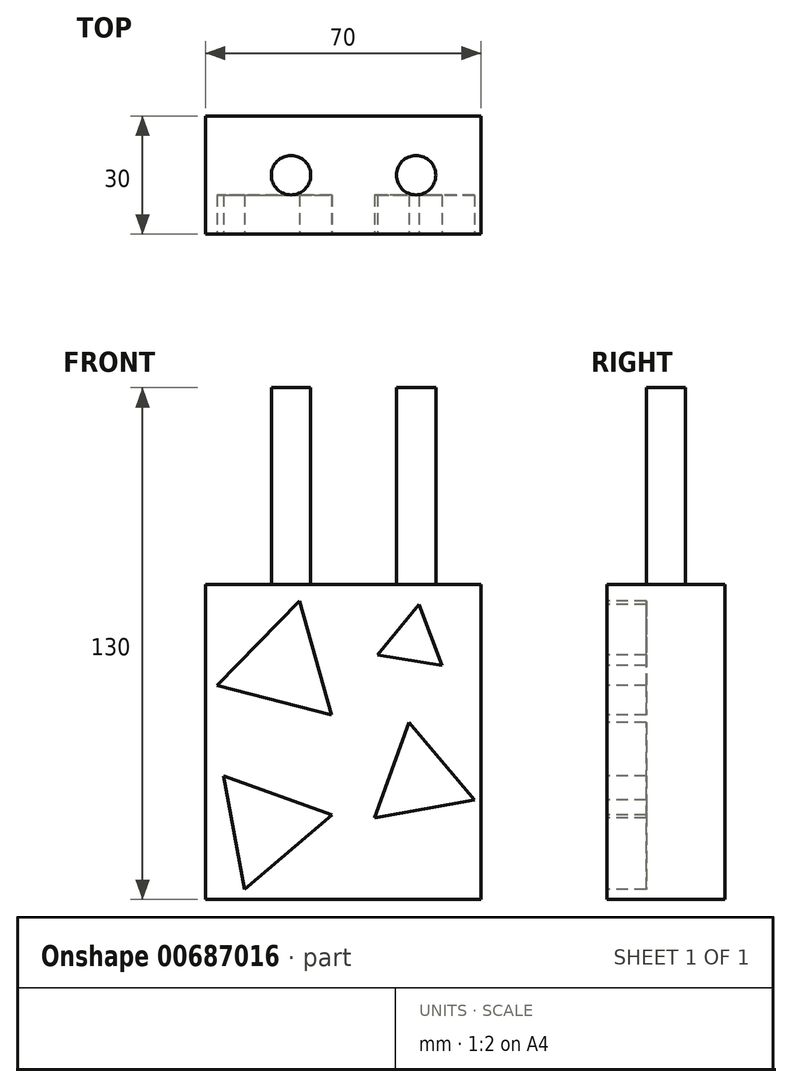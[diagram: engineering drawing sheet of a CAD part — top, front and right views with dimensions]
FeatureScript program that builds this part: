
annotation { "Feature Type Name" : "Feature", "Feature Type Description" : "" }
export const myFeature = defineFeature(function(context is Context, id is Id, definition is map)
    precondition{}
    {
        {
            var Q0;
            Q0=qCreatedBy(makeId("Top.planeOp"),FACE);
            var sketch = newSketch(context, id + "F0", { "sketchPlane" : qUnion([Q0])});
            skLineSegment(sketch, "E0.bottom", {"start": v(35, 15) * mm, "end": v(-35, 15) * mm});
            skLineSegment(sketch, "E0.top", {"start": v(35, -15) * mm, "end": v(-35, -15) * mm});
            skLineSegment(sketch, "E0.left", {"start": v(35, 15) * mm, "end": v(35, -15) * mm});
            skLineSegment(sketch, "E0.right", {"start": v(-35, 15) * mm, "end": v(-35, -15) * mm});
            skPoint(sketch, "E0.middle", {"position": v(0, 0) * mm});
            skSolve(sketch);
        }
        {
            var Q0;
            Q0 = qSketchRegion(id + "F0", true);
            extrude(context, id + "F1", {"entities" : qUnion([Q0]), "depth" : 80 * mm, "offsetDistance" : 25 * mm});
        }
        {
            var Q0;
            Q0=makeQuery(id+"F1.opExtrude","CAP_FACE",FACE,{"disambiguationData":[OSD([sQuery(id+"F0.wireOp",EDGE,"E0.bottom"),sQuery(id+"F0.wireOp",EDGE,"E0.top"),sQuery(id+"F0.wireOp",EDGE,"E0.left"),sQuery(id+"F0.wireOp",EDGE,"E0.right")])],"isStart":false});
            var sketch = newSketch(context, id + "F2", { "sketchPlane" : qUnion([Q0])});
            skCircle(sketch, "E1", {"center": v(-13.25, 0) * mm, "radius": 5 * mm});
            skCircle(sketch, "E2", {"center": v(18.53, 0) * mm, "radius": 5 * mm});
            skSolve(sketch);
        }
        {
            var Q0;
            Q0 = qSketchRegion(id + "F2", true);
            extrude(context, id + "F3", {"entities" : qUnion([Q0]), "operationType" : NewBodyOperationType.ADD, "depth" : 50 * mm, "offsetDistance" : 25 * mm});
        }
        {
            var Q0;
            Q0=makeQuery(id+"F1.opExtrude","SWEPT_FACE",FACE,{"disambiguationData":[OSD([sQuery(id+"F0.wireOp",EDGE,"E0.top")])]});
            var sketch = newSketch(context, id + "F4", { "sketchPlane" : qUnion([Q0])});
            skCircle(sketch, "E3.cCircle", {"center": v(17.68, 65.46) * mm, "radius": 4.8 * mm, "construction": true});
            skLineSegment(sketch, "E3.0", {"start": v(25.12, 59.38) * mm, "end": v(8.7, 62.05) * mm});
            skLineSegment(sketch, "E3.1", {"start": v(8.7, 62.05) * mm, "end": v(19.22, 74.94) * mm});
            skLineSegment(sketch, "E3.2", {"start": v(19.22, 74.94) * mm, "end": v(25.12, 59.38) * mm});
            skPoint(sketch, "E3.0.midPoint", {"position": v(16.9, 60.72) * mm});
            skCircle(sketch, "E4.cCircle", {"center": v(-15.36, 59.04) * mm, "radius": 8.69 * mm, "construction": true});
            skLineSegment(sketch, "E4.0", {"start": v(-11.03, 75.87) * mm, "end": v(-2.94, 46.87) * mm});
            skLineSegment(sketch, "E4.1", {"start": v(-2.94, 46.87) * mm, "end": v(-32.1, 54.36) * mm});
            skLineSegment(sketch, "E4.2", {"start": v(-32.1, 54.36) * mm, "end": v(-11.03, 75.87) * mm});
            skPoint(sketch, "E4.0.midPoint", {"position": v(-6.99, 61.37) * mm});
            skCircle(sketch, "E5.cCircle", {"center": v(-19.44, 18.45) * mm, "radius": 8.45 * mm, "construction": true});
            skLineSegment(sketch, "E5.0", {"start": v(-2.81, 21.5) * mm, "end": v(-25.11, 2.54) * mm});
            skLineSegment(sketch, "E5.1", {"start": v(-25.11, 2.54) * mm, "end": v(-30.38, 31.33) * mm});
            skLineSegment(sketch, "E5.2", {"start": v(-30.38, 31.33) * mm, "end": v(-2.81, 21.5) * mm});
            skPoint(sketch, "E5.0.midPoint", {"position": v(-13.96, 12.02) * mm});
            skCircle(sketch, "E6.cCircle", {"center": v(19.33, 30.32) * mm, "radius": 7.44 * mm, "construction": true});
            skLineSegment(sketch, "E6.0", {"start": v(16.66, 44.95) * mm, "end": v(33.34, 25.32) * mm});
            skLineSegment(sketch, "E6.1", {"start": v(33.34, 25.32) * mm, "end": v(8, 20.7) * mm});
            skLineSegment(sketch, "E6.2", {"start": v(8, 20.7) * mm, "end": v(16.66, 44.95) * mm});
            skPoint(sketch, "E6.0.midPoint", {"position": v(25, 35.14) * mm});
            skSolve(sketch);
        }
        {
            var Q0;
            Q0 = qSketchRegion(id + "F4", true);
            extrude(context, id + "F5", {"entities" : qUnion([Q0]), "operationType" : NewBodyOperationType.REMOVE, "oppositeDirection" : true, "depth" : 10 * mm, "offsetDistance" : 25 * mm});
        }
    });
